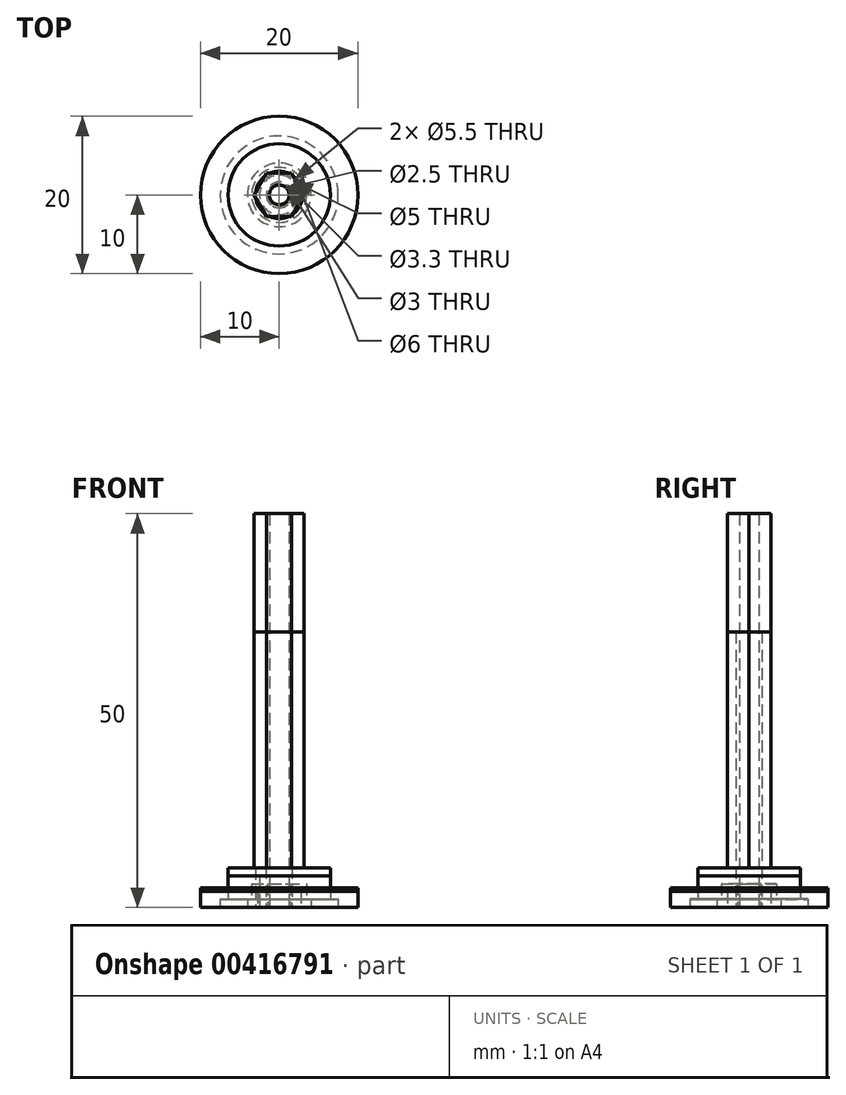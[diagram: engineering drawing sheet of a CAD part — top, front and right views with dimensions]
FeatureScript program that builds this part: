
annotation { "Feature Type Name" : "Feature", "Feature Type Description" : "" }
export const myFeature = defineFeature(function(context is Context, id is Id, definition is map)
    precondition{}
    {
        {
            var Q0;
            Q0=qCreatedBy(makeId("Top.planeOp"),FACE);
            var sketch = newSketch(context, id + "F0", { "sketchPlane" : qUnion([Q0])});
            skCircle(sketch, "E0.cCircle", {"center": v(0, 0) * mm, "radius": 2.75 * mm, "construction": true});
            skLineSegment(sketch, "E0.0", {"start": v(1.59, -2.75) * mm, "end": v(-1.59, -2.75) * mm});
            skLineSegment(sketch, "E0.1", {"start": v(-1.59, -2.75) * mm, "end": v(-3.18, 0) * mm});
            skLineSegment(sketch, "E0.2", {"start": v(-3.18, 0) * mm, "end": v(-1.59, 2.75) * mm});
            skLineSegment(sketch, "E0.3", {"start": v(-1.59, 2.75) * mm, "end": v(1.59, 2.75) * mm});
            skLineSegment(sketch, "E0.4", {"start": v(1.59, 2.75) * mm, "end": v(3.18, 0) * mm});
            skLineSegment(sketch, "E0.5", {"start": v(3.18, 0) * mm, "end": v(1.59, -2.75) * mm});
            skPoint(sketch, "E0.0.midPoint", {"position": v(0, -2.75) * mm});
            skSolve(sketch);
        }
        {
            var Q0;
            Q0=makeQuery(id+"F0.imprint","IMPRINT",FACE,{"disambiguationData":[TD([[makeQuery(id+"F0.imprint","IMPRINT",EDGE,{"derivedFrom":sQuery(id+"F0.wireOp",EDGE,"E0.0")}),-1.0]])]});
            extrude(context, id + "F1", {"entities" : qUnion([Q0]), "depth" : 50 * mm});
        }
        {
            var Q0;
            Q0=sQuery(id+"F0.wireOp",VERTEX,"E0.cCircle.center");
            var Q1;
            Q1=makeQuery(id+"F1.opExtrude","SWEPT_BODY",BODY,{"disambiguationData":[OSD([sQuery(id+"F0.wireOp",EDGE,"E0.0"),sQuery(id+"F0.wireOp",EDGE,"E0.1"),sQuery(id+"F0.wireOp",EDGE,"E0.2"),sQuery(id+"F0.wireOp",EDGE,"E0.3"),sQuery(id+"F0.wireOp",EDGE,"E0.4"),sQuery(id+"F0.wireOp",EDGE,"E0.5")])]});
            hole(context, id + "F2", {"style" : HoleStyle.SIMPLE, "endStyle" : HoleEndStyle.THROUGH, "oppositeDirection" : true, "standardTappedOrClearance" : lookupTablePath({ "standard" : "ISO", "engagement" : "75%", "pitch" : "0.5 mm", "size" : "M3", "type" : "Tapped" }), "standardBlindInLast" : lookupTablePath({ "standard" : "ISO", "engagement" : "75%", "pitch" : "0.5 mm", "size" : "M3", "type" : "Tapped" }), "holeDiameter" : 2.5 * mm, "showTappedDepth" : true, "isTappedThrough" : true, "tappedDepth" : 6.2 * mm, "tapClearance" : 3, "locations" : qUnion([Q0]), "scope" : qUnion([Q1]), "majorDiameter" : 3 * mm});
        }
        {
            var Q0;
            Q0=qCreatedBy(makeId("Front.planeOp"),FACE);
            var sketch = newSketch(context, id + "F3", { "sketchPlane" : qUnion([Q0])});
            skLineSegment(sketch, "E1", {"start": v(0, 0) * mm, "end": v(0, 7.5) * mm, "construction": true});
            skLineSegment(sketch, "E2", {"start": v(-6.5, 5) * mm, "end": v(-6.5, 1.1) * mm});
            skLineSegment(sketch, "E3", {"start": v(-6.5, 1.1) * mm, "end": v(-7.5, 1.1) * mm});
            skLineSegment(sketch, "E4", {"start": v(-7.5, 1.1) * mm, "end": v(-7.5, 0) * mm});
            skLineSegment(sketch, "E5", {"start": v(-6.5, 5) * mm, "end": v(-3, 5) * mm});
            skLineSegment(sketch, "E6", {"start": v(-7.5, 0) * mm, "end": v(-3, 0) * mm});
            skLineSegment(sketch, "E7", {"start": v(-3, 0) * mm, "end": v(-3, 5) * mm});
            skSolve(sketch);
        }
        {
            var Q0;
            Q0 = qSketchRegion(id + "F3", true);
            var Q1;
            Q1=sQuery(id+"F3.wireOp",EDGE,"E1");
            revolve(context, id + "F4", {"entities" : qUnion([Q0]), "axis" : qUnion([Q1]), "revolveType" : RevolveType.FULL});
        }
        {
            var Q0;
            Q0=qCreatedBy(makeId("Front.planeOp"),FACE);
            var sketch = newSketch(context, id + "F5", { "sketchPlane" : qUnion([Q0])});
            skLineSegment(sketch, "E8", {"start": v(0, 0) * mm, "end": v(0, 7.1) * mm, "construction": true});
            skLineSegment(sketch, "E9", {"start": v(-2.5, 0) * mm, "end": v(-2.5, 4) * mm});
            skLineSegment(sketch, "E10", {"start": v(-2.5, 4) * mm, "end": v(-6.5, 4) * mm});
            skLineSegment(sketch, "E11", {"start": v(-6.5, 4) * mm, "end": v(-6.5, 1) * mm});
            skLineSegment(sketch, "E12", {"start": v(-6.5, 1) * mm, "end": v(-7.5, 1) * mm});
            skLineSegment(sketch, "E13", {"start": v(-7.5, 1) * mm, "end": v(-7.5, 0) * mm});
            skLineSegment(sketch, "E14", {"start": v(-7.5, 0) * mm, "end": v(-2.5, 0) * mm});
            skSolve(sketch);
        }
        {
            var Q0;
            Q0 = qSketchRegion(id + "F5", true);
            var Q1;
            Q1=sQuery(id+"F5.wireOp",EDGE,"E8");
            revolve(context, id + "F6", {"entities" : qUnion([Q0]), "axis" : qUnion([Q1]), "revolveType" : RevolveType.FULL});
        }
        {
            var Q0;
            Q0 = qSketchRegion(id + "F0", true);
            extrude(context, id + "F7", {"entities" : qUnion([Q0]), "depth" : 35 * mm});
        }
        {
            var Q0;
            Q0=sQuery(id+"F0.wireOp",VERTEX,"E0.cCircle.center");
            var Q1;
            Q1=makeQuery(id+"F7.opExtrude","SWEPT_BODY",BODY,{"disambiguationData":[OSD([sQuery(id+"F0.wireOp",EDGE,"E0.0"),sQuery(id+"F0.wireOp",EDGE,"E0.1"),sQuery(id+"F0.wireOp",EDGE,"E0.2"),sQuery(id+"F0.wireOp",EDGE,"E0.3"),sQuery(id+"F0.wireOp",EDGE,"E0.4"),sQuery(id+"F0.wireOp",EDGE,"E0.5")])]});
            hole(context, id + "F8", {"style" : HoleStyle.SIMPLE, "endStyle" : HoleEndStyle.THROUGH, "oppositeDirection" : true, "standardTappedOrClearance" : lookupTablePath({ "standard" : "ISO", "fit" : "Normal", "size" : "M3", "type" : "Clearance" }), "standardBlindInLast" : lookupTablePath({ "fit" : "Standard", "standard" : "ISO", "size" : "M3", "type" : "Clearance" }), "holeDiameter" : 3.3 * mm, "isTappedThrough" : true, "tappedDepth" : 6.2 * mm, "tapClearance" : 3, "locations" : qUnion([Q0]), "scope" : qUnion([Q1])});
        }
        {
            var Q0;
            Q0=qCreatedBy(makeId("Front.planeOp"),FACE);
            var sketch = newSketch(context, id + "F9", { "sketchPlane" : qUnion([Q0])});
            skLineSegment(sketch, "E15", {"start": v(0, 0) * mm, "end": v(0, 4.3) * mm, "construction": true});
            skLineSegment(sketch, "E16", {"start": v(-1.5, 0) * mm, "end": v(-1.5, 3) * mm});
            skLineSegment(sketch, "E17", {"start": v(-1.5, 3) * mm, "end": v(-3.5, 3) * mm});
            skLineSegment(sketch, "E18", {"start": v(-3.5, 3) * mm, "end": v(-3.5, 1) * mm});
            skLineSegment(sketch, "E19", {"start": v(-3.5, 1) * mm, "end": v(-4.05, 1) * mm});
            skLineSegment(sketch, "E20", {"start": v(-4.05, 1) * mm, "end": v(-4.05, 0) * mm});
            skLineSegment(sketch, "E21", {"start": v(-4.05, 0) * mm, "end": v(-1.5, 0) * mm});
            skSolve(sketch);
        }
        {
            var Q0;
            Q0=makeQuery(id+"F9.imprint","IMPRINT",FACE,{"disambiguationData":[TD([[makeQuery(id+"F9.imprint","IMPRINT",EDGE,{"derivedFrom":sQuery(id+"F9.wireOp",EDGE,"E16")}),1.0]])]});
            var Q1;
            Q1=sQuery(id+"F9.wireOp",EDGE,"E15");
            revolve(context, id + "F10", {"entities" : qUnion([Q0]), "axis" : qUnion([Q1]), "revolveType" : RevolveType.FULL});
        }
        {
            var Q0;
            Q0=qCreatedBy(makeId("Top.planeOp"),FACE);
            var sketch = newSketch(context, id + "F11", { "sketchPlane" : qUnion([Q0])});
            skCircle(sketch, "E22", {"center": v(0, 0) * mm, "radius": 10 * mm});
            skCircle(sketch, "E23", {"center": v(0, 0) * mm, "radius": 2.75 * mm});
            skSolve(sketch);
        }
        {
            var Q0;
            Q0=makeQuery(id+"F11.imprint","IMPRINT",FACE,{"disambiguationData":[TD([[makeQuery(id+"F11.imprint","IMPRINT",EDGE,{"derivedFrom":sQuery(id+"F11.wireOp",EDGE,"E22")}),1.0]])]});
            extrude(context, id + "F12", {"entities" : qUnion([Q0]), "depth" : 2.5 * mm});
        }
        {
            var Q0;
            Q0 = qSketchRegion(id + "F11", true);
            extrude(context, id + "F13", {"entities" : qUnion([Q0]), "depth" : 2 * mm});
        }
    });
